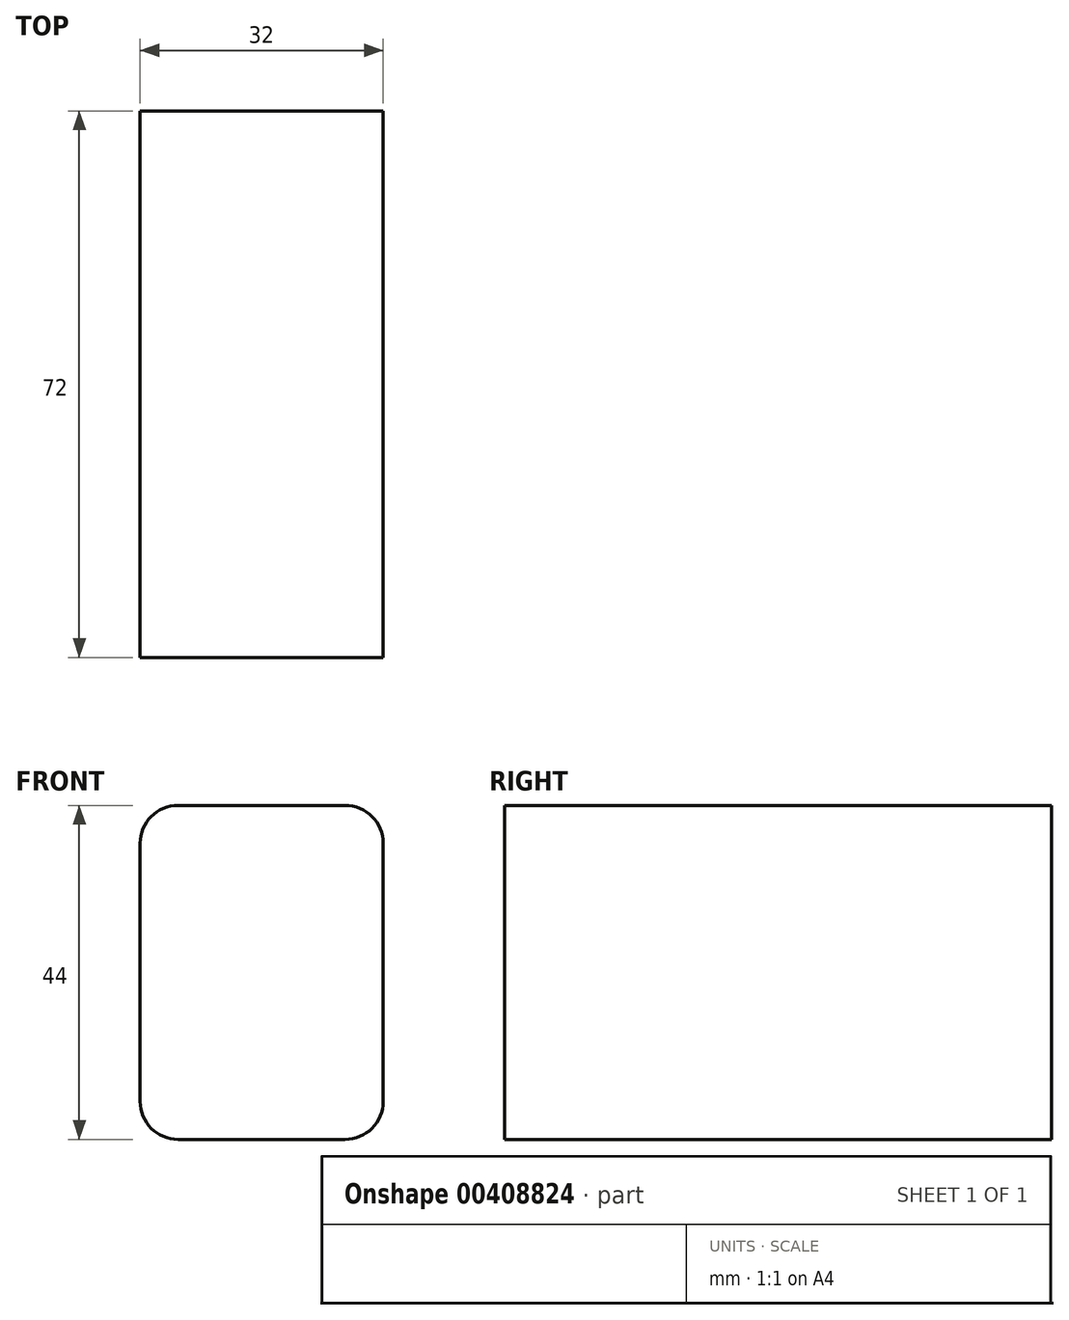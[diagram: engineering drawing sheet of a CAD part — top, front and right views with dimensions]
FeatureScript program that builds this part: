
annotation { "Feature Type Name" : "Feature", "Feature Type Description" : "" }
export const myFeature = defineFeature(function(context is Context, id is Id, definition is map)
    precondition{}
    {
        {
            var Q0;
            Q0=qCreatedBy(makeId("Top.planeOp"),FACE);
            var sketch = newSketch(context, id + "F0", { "sketchPlane" : qUnion([Q0])});
            skLineSegment(sketch, "E0.bottom", {"start": v(-16, 36) * mm, "end": v(16, 36) * mm});
            skLineSegment(sketch, "E0.top", {"start": v(-16, -36) * mm, "end": v(16, -36) * mm});
            skLineSegment(sketch, "E0.left", {"start": v(-16, 36) * mm, "end": v(-16, -36) * mm});
            skLineSegment(sketch, "E0.right", {"start": v(16, 36) * mm, "end": v(16, -36) * mm});
            skPoint(sketch, "E0.middle", {"position": v(0, 0) * mm});
            skSolve(sketch);
        }
        {
            var Q0;
            Q0=makeQuery(id+"F0.imprint","IMPRINT",FACE,{"disambiguationData":[TD([[makeQuery(id+"F0.imprint","IMPRINT",EDGE,{"derivedFrom":sQuery(id+"F0.wireOp",EDGE,"E0.bottom")}),-1.0]])]});
            extrude(context, id + "F1", {"entities" : qUnion([Q0]), "depth" : 44 * mm});
        }
        {
            var Q0;
            Q0=makeQuery(id+"F1.opExtrude","CAP_EDGE",EDGE,{"disambiguationData":[OSD([sQuery(id+"F0.wireOp",EDGE,"E0.right")])],"isStart":false});
            var Q1;
            Q1=makeQuery(id+"F1.opExtrude","CAP_EDGE",EDGE,{"disambiguationData":[OSD([sQuery(id+"F0.wireOp",EDGE,"E0.left")])],"isStart":false});
            var Q2;
            Q2=makeQuery(id+"F1.opExtrude","CAP_EDGE",EDGE,{"disambiguationData":[OSD([sQuery(id+"F0.wireOp",EDGE,"E0.right")])],"isStart":true});
            var Q3;
            Q3=makeQuery(id+"F1.opExtrude","CAP_EDGE",EDGE,{"disambiguationData":[OSD([sQuery(id+"F0.wireOp",EDGE,"E0.left")])],"isStart":true});
            fillet(context, id + "F2", {"entities" : qUnion([Q0, Q1, Q2, Q3]), "radius" : 5 * mm, "tangentPropagation" : true, "allowEdgeOverflow" : false});
        }
    });
